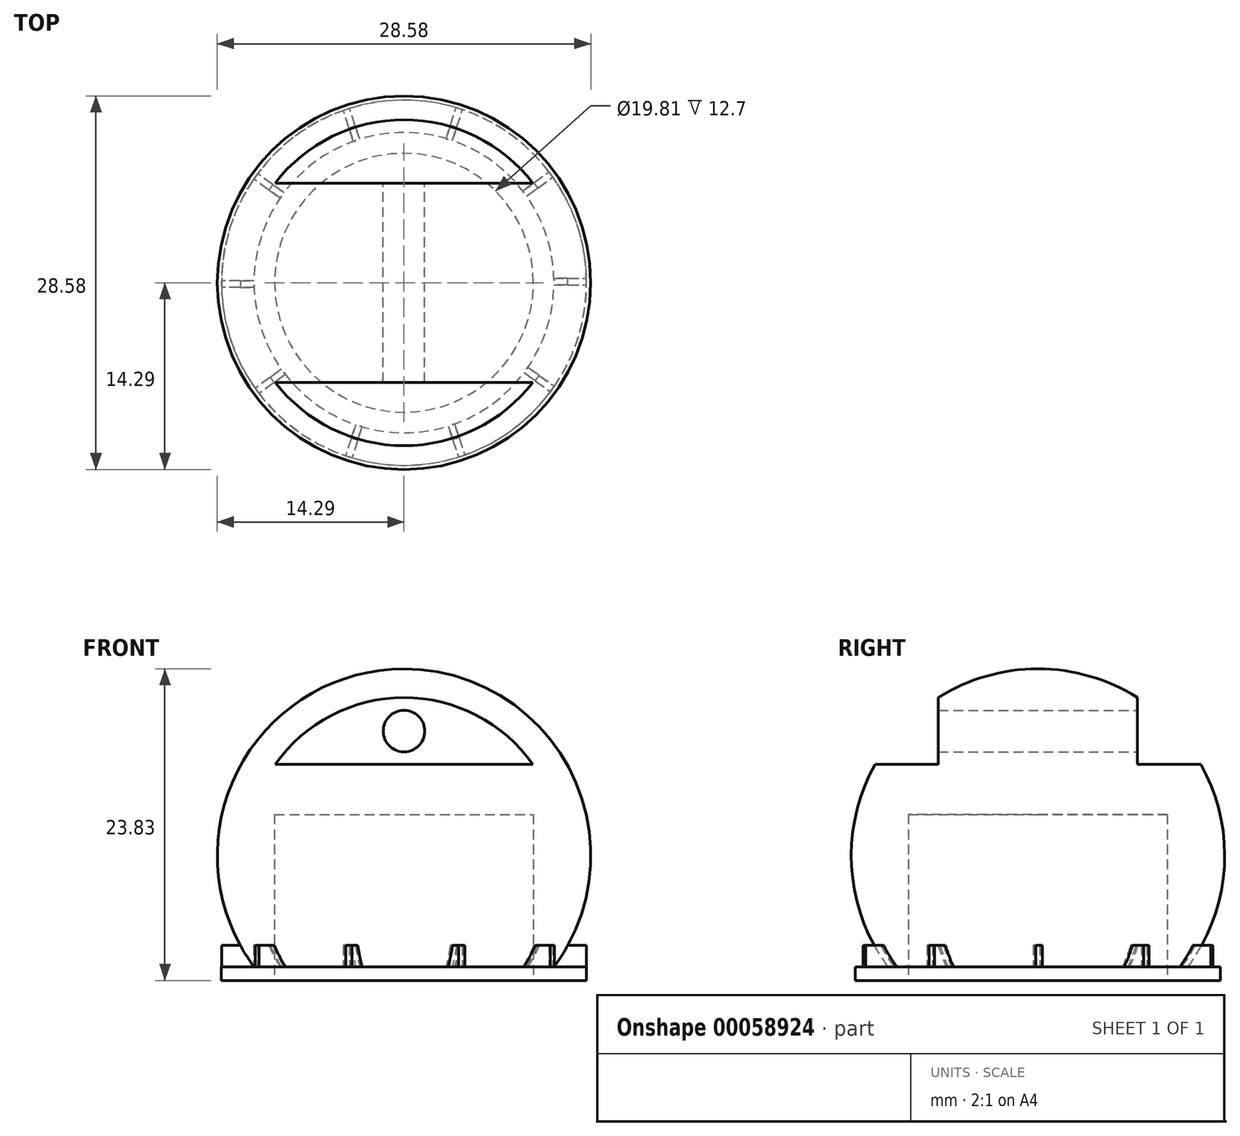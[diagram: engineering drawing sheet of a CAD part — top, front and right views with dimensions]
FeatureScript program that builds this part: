
annotation { "Feature Type Name" : "Feature", "Feature Type Description" : "" }
export const myFeature = defineFeature(function(context is Context, id is Id, definition is map)
    precondition{}
    {
        {
            var Q0;
            Q0=qCreatedBy(makeId("Front.planeOp"),FACE);
            var sketch = newSketch(context, id + "F0", { "sketchPlane" : qUnion([Q0])});
            skArc(sketch, "E0", {"start": v(-45.67, 1.02) * mm, "mid": v(-57.15, 23.81) * mm, "end": v(-68.63, 1.02) * mm});
            skLineSegment(sketch, "E1", {"start": v(-57.15, 40.83) * mm, "end": v(-57.15, -8.86) * mm, "construction": true});
            skLineSegment(sketch, "E2.rect.bottom", {"start": v(-71.12, 1.02) * mm, "end": v(-68.63, 1.02) * mm});
            skLineSegment(sketch, "E2.rect.top", {"start": v(-71.12, -0.02) * mm, "end": v(-43.18, -0.02) * mm});
            skLineSegment(sketch, "E2.rect.left", {"start": v(-71.12, 1.02) * mm, "end": v(-71.12, -0.02) * mm});
            skLineSegment(sketch, "E2.rect.right", {"start": v(-43.18, 1.02) * mm, "end": v(-43.18, -0.02) * mm});
            skPoint(sketch, "E2.rect.middle", {"position": v(-57.15, 0.5) * mm});
            skLineSegment(sketch, "E3.trimOffspring", {"start": v(-45.67, 1.02) * mm, "end": v(-43.18, 1.02) * mm});
            skLineSegment(sketch, "E4", {"start": v(-57.15, -0.02) * mm, "end": v(-57.15, 23.81) * mm});
            skSolve(sketch);
        }
        {
            var Q0;
            {var subQ1=sQuery(id+"F0.wireOp",EDGE,"E2.rect.right");Q0=makeQuery(id+"F0.imprint","IMPRINT",FACE,{"disambiguationData":[TD([[makeQuery(id+"F0.imprint","IMPRINT",EDGE,{"derivedFrom":subQ1}),-1.0]])]});}
            var Q1;
            Q1=sQuery(id+"F0.wireOp",EDGE,"E4");
            revolve(context, id + "F1", {"entities" : qUnion([Q0]), "axis" : qUnion([Q1]), "revolveType" : RevolveType.FULL});
        }
        {
            var Q0;
            Q0=makeQuery(id+"F1.opRevolve","SWEPT_FACE",FACE,{"disambiguationData":[OSD([sQuery(id+"F0.wireOp",EDGE,"E3.trimOffspring")])]});
            var sketch = newSketch(context, id + "F2", { "sketchPlane" : qUnion([Q0])});
            skLineSegment(sketch, "E5.bottom", {"start": v(-45.67, -0.16) * mm, "end": v(-43.18, -0.16) * mm});
            skLineSegment(sketch, "E5.top", {"start": v(-45.67, 0.34) * mm, "end": v(-43.18, 0.34) * mm});
            skLineSegment(sketch, "E5.left", {"start": v(-45.67, -0.16) * mm, "end": v(-45.67, 0.34) * mm});
            skLineSegment(sketch, "E5.right", {"start": v(-43.18, -0.16) * mm, "end": v(-43.18, 0.34) * mm});
            skSolve(sketch);
        }
        {
            var Q0;
            {var subQ4=sQuery(id+"F2.wireOp",EDGE,"E5.bottom");Q0=makeQuery(id+"F2.imprint","IMPRINT",FACE,{"disambiguationData":[TD([[makeQuery(id+"F2.imprint","IMPRINT",EDGE,{"derivedFrom":subQ4}),1.0]])]});}
            extrude(context, id + "F3", {"entities" : qUnion([Q0]), "operationType" : NewBodyOperationType.ADD, "depth" : 1.65 * mm});
        }
        {
            var Q0;
            Q0=makeQuery(id+"F1.opRevolve","SWEPT_BODY",BODY,{"disambiguationData":[OSD([sQuery(id+"F0.wireOp",EDGE,"E0"),sQuery(id+"F0.wireOp",EDGE,"E2.rect.top"),sQuery(id+"F0.wireOp",EDGE,"E2.rect.right"),sQuery(id+"F0.wireOp",EDGE,"E3.trimOffspring"),sQuery(id+"F0.wireOp",EDGE,"E4")])]});
            var Q1;
            Q1=makeQuery(id+"F3.opExtrude","SWEPT_FACE",FACE,{"disambiguationData":[OSD([sQuery(id+"F2.wireOp",EDGE,"E5.right")])]});
            var Q2;
            Q2=makeQuery(id+"F3.opExtrude","SWEPT_FACE",FACE,{"disambiguationData":[OSD([sQuery(id+"F2.wireOp",EDGE,"E5.bottom")])]});
            var Q3;
            Q3=makeQuery(id+"F3.opExtrude","CAP_FACE",FACE,{"disambiguationData":[OSD([sQuery(id+"F0.wireOp",EDGE,"E0"),sQuery(id+"F0.wireOp",EDGE,"E3.trimOffspring"),sQuery(id+"F2.wireOp",EDGE,"E5.bottom"),sQuery(id+"F2.wireOp",EDGE,"E5.top"),sQuery(id+"F2.wireOp",EDGE,"E5.left"),sQuery(id+"F2.wireOp",EDGE,"E5.right")])],"isStart":false});
            var Q4;
            Q4=makeQuery(id+"F3.opExtrude","SWEPT_FACE",FACE,{"disambiguationData":[OSD([sQuery(id+"F2.wireOp",EDGE,"E5.top")])]});
            var Q5;
            Q5=makeQuery(id+"F3.opExtrude","SWEPT_FACE",FACE,{"disambiguationData":[OSD([sQuery(id+"F2.wireOp",EDGE,"E5.left")])]});
            var Q6;
            Q6=makeQuery(id+"F1.opRevolve","SWEPT_EDGE",EDGE,{"disambiguationData":[OSD([sQuery(id+"F0.wireOp",EDGE,"E2.rect.right"),sQuery(id+"F0.wireOp",EDGE,"E3.trimOffspring")])]});
            circularPattern(context, id + "F4", {"faces" : qUnion([Q1, Q2, Q3, Q4, Q5]), "axis" : qUnion([Q6]), "angle" : 360 * degree, "instanceCount" : 10, "equalSpace" : true, "patternType" : PatternType.FACE});
        }
        {
            var Q0;
            Q0=qCreatedBy(makeId("Top.planeOp"),FACE);
            cPlane(context, id + "F5", {"entities" : qUnion([Q0]), "cplaneType" : CPlaneType.OFFSET, "offset" : 16.5 * mm, "width" : 152.4 * mm, "height" : 152.4 * mm});
        }
        {
            var Q0;
            Q0=qCreatedBy(id+"F5.planeOp",FACE);
            var sketch = newSketch(context, id + "F6", { "sketchPlane" : qUnion([Q0])});
            skLineSegment(sketch, "E6.bottom", {"start": v(-44.45, -7.62) * mm, "end": v(-69.85, -7.62) * mm});
            skLineSegment(sketch, "E6.top", {"start": v(-44.45, -12.7) * mm, "end": v(-69.85, -12.7) * mm});
            skLineSegment(sketch, "E6.left", {"start": v(-44.45, -7.62) * mm, "end": v(-44.45, -12.7) * mm});
            skLineSegment(sketch, "E6.right", {"start": v(-69.85, -7.62) * mm, "end": v(-69.85, -12.7) * mm});
            skLineSegment(sketch, "E7.bottom", {"start": v(-44.45, 12.7) * mm, "end": v(-69.85, 12.7) * mm});
            skLineSegment(sketch, "E7.top", {"start": v(-44.45, 7.62) * mm, "end": v(-69.85, 7.62) * mm});
            skLineSegment(sketch, "E7.left", {"start": v(-44.45, 12.7) * mm, "end": v(-44.45, 7.62) * mm});
            skLineSegment(sketch, "E7.right", {"start": v(-69.85, 12.7) * mm, "end": v(-69.85, 7.62) * mm});
            skSolve(sketch);
        }
        {
            var Q0;
            Q0=makeQuery(id+"F6.imprint","IMPRINT",FACE,{"disambiguationData":[TD([[makeQuery(id+"F6.imprint","IMPRINT",EDGE,{"derivedFrom":sQuery(id+"F6.wireOp",EDGE,"E7.bottom")}),1.0]])]});
            var Q1;
            Q1=makeQuery(id+"F6.imprint","IMPRINT",FACE,{"disambiguationData":[TD([[makeQuery(id+"F6.imprint","IMPRINT",EDGE,{"derivedFrom":sQuery(id+"F6.wireOp",EDGE,"E6.bottom")}),1.0]])]});
            extrude(context, id + "F7", {"entities" : qUnion([Q0, Q1]), "operationType" : NewBodyOperationType.REMOVE, "depth" : 6.35 * mm});
        }
        {
            var Q0;
            Q0=makeQuery(id+"F7.boolean.opBoolean","COPY",FACE,{"derivedFrom":makeQuery(id+"F7.opExtrude","SWEPT_FACE",FACE,{"disambiguationData":[OSD([sQuery(id+"F6.wireOp",EDGE,"E6.bottom")])]})});
            var sketch = newSketch(context, id + "F8", { "sketchPlane" : qUnion([Q0])});
            skCircle(sketch, "E8", {"center": v(-57.15, 19.05) * mm, "radius": 1.59 * mm});
            skSolve(sketch);
        }
        {
            var Q0;
            Q0=makeQuery(id+"F8.imprint","IMPRINT",FACE,{"disambiguationData":[TD([[makeQuery(id+"F8.imprint","IMPRINT",EDGE,{"derivedFrom":sQuery(id+"F8.wireOp",EDGE,"E8")}),1.0]])]});
            extrude(context, id + "F9", {"entities" : qUnion([Q0]), "operationType" : NewBodyOperationType.REMOVE, "depth" : 3.8 * mm, "hasSecondDirection" : true, "secondDirectionOppositeDirection" : true, "secondDirectionDepth" : 19.05 * mm});
        }
        {
            var Q0;
            Q0=makeQuery(id+"F1.opRevolve","SWEPT_FACE",FACE,{"disambiguationData":[OSD([sQuery(id+"F0.wireOp",EDGE,"E2.rect.top")])]});
            var sketch = newSketch(context, id + "F10", { "sketchPlane" : qUnion([Q0])});
            skCircle(sketch, "E9", {"center": v(-57.15, 0) * mm, "radius": 9.9 * mm});
            skSolve(sketch);
        }
        {
            var Q0;
            Q0=makeQuery(id+"F10.imprint","IMPRINT",FACE,{"disambiguationData":[TD([[makeQuery(id+"F10.imprint","IMPRINT",EDGE,{"derivedFrom":sQuery(id+"F10.wireOp",EDGE,"E9")}),1.0]])]});
            extrude(context, id + "F11", {"entities" : qUnion([Q0]), "operationType" : NewBodyOperationType.REMOVE, "oppositeDirection" : true, "depth" : 12.7 * mm});
        }
        {
            var Q0;
            Q0=qCreatedBy(makeId("Top.planeOp"),FACE);
            var sketch = newSketch(context, id + "F12", { "sketchPlane" : qUnion([Q0])});
            skCircle(sketch, "E10", {"center": v(0, 0) * mm, "radius": 9.53 * mm});
            skSolve(sketch);
        }
        {
            var Q0;
            Q0=makeQuery(id+"F12.imprint","IMPRINT",FACE,{"disambiguationData":[TD([[makeQuery(id+"F12.imprint","IMPRINT",EDGE,{"derivedFrom":sQuery(id+"F12.wireOp",EDGE,"E10")}),1.0]])]});
            extrude(context, id + "F13", {"entities" : qUnion([Q0]), "depth" : 57.15 * mm});
        }
        {
            var Q0;
            Q0=makeQuery(id+"F13.opExtrude","CAP_FACE",FACE,{"disambiguationData":[OSD([sQuery(id+"F12.wireOp",EDGE,"E10")])],"isStart":true});
            var sketch = newSketch(context, id + "F14", { "sketchPlane" : qUnion([Q0])});
            skPoint(sketch, "E11", {"position": v(0, 0) * mm});
            skCircle(sketch, "E12", {"center": v(0, 0) * mm, "radius": 7.62 * mm});
            skSolve(sketch);
        }
        {
            var Q0;
            Q0=makeQuery(id+"F14.imprint","IMPRINT",FACE,{"disambiguationData":[TD([[makeQuery(id+"F14.imprint","IMPRINT",EDGE,{"derivedFrom":sQuery(id+"F14.wireOp",EDGE,"E12")}),1.0]])]});
            extrude(context, id + "F15", {"entities" : qUnion([Q0]), "operationType" : NewBodyOperationType.REMOVE, "oppositeDirection" : true, "depth" : 44.45 * mm});
        }
        {
            var Q0;
            Q0=makeQuery(id+"F13.opExtrude","SWEPT_BODY",BODY,{"disambiguationData":[OSD([sQuery(id+"F12.wireOp",EDGE,"E10")])]});
            deleteBodies(context, id + "F16", {"entities" : qUnion([Q0])});
        }
    });
